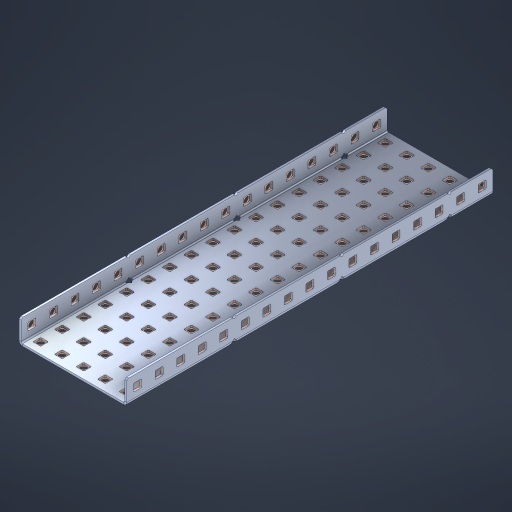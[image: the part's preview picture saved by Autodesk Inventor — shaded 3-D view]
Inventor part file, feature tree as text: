
AUTODESK INVENTOR PART (.ipt)
format: ipt  version: 2023 (Build 270158000, 158)  size: 1,493,504 bytes
history: native  units: in
note: dims shown in document units (in); Inventor stores cm internally (conversion verified against a paired STEP export)
features: other x124, extrude x118, sheet_metal_op x10, sketch x8, mirror x1, pattern_linear x1, chamfer x1
ambient origin geometry x8: Origin, YZ Plane, XZ Plane, XY Plane, X Axis, Y Axis, Z Axis, Center Point
bodies: Solid1 (feature_tree), Body (feature_tree)
feature tree (263):
  other  "Flange Pattern Plane"
  sheet_metal_op  "Flange Pattern"
  sheet_metal_op  "Body Pattern"
  other  "Arc Length"
  mirror  "Notch Mirror"
  pattern_linear  "Notch Pattern"  Spacing1=0.1875in  [1 undecoded]
  chamfer  "End Chamfer"
  extrude  "Half Cut"  Depth=0.0469in
  sketch  "Sketch1"  dims[d0=2.5in]
  other  "Plate1"
  sketch  "Sketch2"  dims[d1=8.5in]
  other  "Plate2"
  sheet_metal_op  "Bend1"
  sheet_metal_op  "Corner1"
  sketch  "Sketch3"  dims[d2=0.0469in]
  other  "Flange Pattern Sketch"
  sketch  "Sketch7"  dims[d3=0.0469in]
  other  "Srf1"
  other  "Srf2"
  sketch  "Sketch8"  dims[d4=0.0234in]
  sketch  "Sketch9"  dims[d5=0.0938in]
  other  "Srf91"
  sheet_metal_op  "Body Pattern Sketch"
  other  "Srf92"
  sketch  "Sketch13"  dims[d6=0.0469in]
  sketch  "Sketch14"  dims[d7=0.5in d8=90.0deg d9=0.0312in d10=0.1875in d11=0.0469in d12=0.0469in d16=0.182in d17=0.02in d18=0.0469in d19=0.0in d20=0.25in d21=0.25in d46=0.172in d47=1.0in d48=0.0in d49=0.182in d50=0.02in d51=0.25in d52=0.25in d53=0.0469in d54=0.0in d55=0.172in d56=1.0in d57=0.0in d60=6.6929in d62=0.5in d63=1.9685in d65=0.5in d85=0.1227in d86=0.1659in d88=0.04in d89=0.0469in d90=0.0in d91=0.04in d92=0.0491in d95=2.5in d96=0.04in d97=0.25in d98=45.0deg d101=0.0in d102=2.497in d131=2.5in d132=6.6929in d134=0.5in d139=0.5in]
  other  "Srf856"
  other  "Srf1310"
  other  "Srf1311"
  other  "Srf1312"
  other  "Srf1376"
  other  "Srf1377"
  other  "Srf1728"
  other  "Srf1755"
  other  "Srf1878"
  other  "Srf1879"
  other  "Srf1880"
  other  "Srf1881"
  other  "Srf1882"
  other  "Srf1883"
  other  "Srf1884"
  other  "Srf1885"
  other  "Srf1886"
  other  "Srf1887"
  other  "Srf1888"
  other  "Srf1889"
  other  "Srf1890"
  other  "Srf1891"
  other  "Srf1892"
  other  "Srf1893"
  other  "Srf1894"
  other  "Srf1895"
  other  "Srf1896"
  other  "Srf1897"
  other  "Srf1898"
  other  "Srf1899"
  other  "Srf1900"
  other  "Srf1901"
  other  "Srf1902"
  other  "Srf1903"
  other  "Srf1904"
  other  "Srf1905"
  other  "Srf1942"
  other  "Srf1943"
  other  "Srf1944"
  other  "Srf1945"
  other  "Srf1946"
  other  "Srf1947"
  other  "Srf1948"
  other  "Srf1949"
  other  "Srf1950"
  other  "Srf1951"
  other  "Srf1952"
  other  "Srf1953"
  other  "Srf1954"
  other  "Srf1955"
  other  "Srf1956"
  other  "Srf1957"
  other  "Srf1958"
  other  "Srf1959"
  other  "Srf1960"
  other  "Srf1961"
  other  "Srf1962"
  other  "Srf1963"
  other  "Srf1964"
  other  "Srf1965"
  other  "Srf1966"
  other  "Srf1967"
  other  "Srf1968"
  other  "Srf1969"
  other  "Srf1970"
  other  "Srf2146"
  other  "Srf2147"
  other  "Srf2148"
  other  "Srf2149"
  other  "Srf2150"
  other  "Srf2151"
  other  "Srf2152"
  other  "Srf2153"
  other  "Srf2154"
  other  "Srf2155"
  other  "Srf2156"
  other  "Srf2157"
  other  "Srf2158"
  other  "Srf2159"
  other  "Srf2160"
  other  "Srf2161"
  other  "Srf2162"
  other  "Srf2163"
  other  "Srf2164"
  other  "Srf2165"
  other  "Srf2166"
  other  "Srf2167"
  other  "Srf2168"
  other  "Srf2169"
  other  "Srf2170"
  other  "Srf2171"
  other  "Srf2172"
  other  "Srf2173"
  other  "Srf2174"
  other  "Srf2175"
  other  "Srf2176"
  other  "Srf2177"
  other  "Srf2178"
  other  "Srf2179"
  other  "Srf2180"
  other  "Srf2181"
  other  "Srf2182"
  other  "Srf2183"
  other  "Srf2184"
  other  "Srf2185"
  other  "Srf2186"
  other  "Srf2187"
  other  "Srf2188"
  other  "Srf2189"
  other  "Srf2190"
  other  "Srf2191"
  other  "Srf2192"
  other  "Srf2193"
  other  "Srf2194"
  other  "Srf2195"
  sheet_metal_op  "Flange Stamp"
  sheet_metal_op  "Flange Circle"
  sheet_metal_op  "Body Stamp"
  sheet_metal_op  "Body Circle"
  sheet_metal_op  "Notch"
  extrude  "ExtrusionSrf2"  Depth=0.0469in
  extrude  "ExtrusionSrf92"  Depth=2.5in
  extrude  "ExtrusionSrf856"  Depth=0.02in
  extrude  "ExtrusionSrf1310"  Depth=0.0469in
  extrude  "ExtrusionSrf1311"  TaperAngle=0.0deg  [1 undecoded]
  extrude  "ExtrusionSrf1312"  Depth=0.25in
  extrude  "ExtrusionSrf1376"  Depth=0.25in
  extrude  "ExtrusionSrf1377"  Depth=2.5in
  extrude  "ExtrusionSrf1728"  Depth=2.5in TaperAngle=0.0deg
  extrude  "ExtrusionSrf1755"  Depth=2.5in
  extrude  "ExtrusionSrf1878"  Depth=0.02in
  extrude  "ExtrusionSrf1879"  Depth=0.25in
  extrude  "ExtrusionSrf1880"  Depth=0.25in
  extrude  "ExtrusionSrf1881"  Depth=0.0469in
  extrude  "ExtrusionSrf1882"  TaperAngle=0.0deg  [1 undecoded]
  extrude  "ExtrusionSrf1883"  Depth=2.5in
  extrude  "ExtrusionSrf1884"  Depth=2.5in TaperAngle=0.0deg
  extrude  "ExtrusionSrf1885"  Depth=2.5in
  extrude  "ExtrusionSrf1886"  Depth=2.5in
  extrude  "ExtrusionSrf1887"  Depth=2.5in
  extrude  "ExtrusionSrf1888"  Depth=2.5in
  extrude  "ExtrusionSrf1889"  Depth=2.5in
  extrude  "ExtrusionSrf1890"  Depth=0.0469in
  extrude  "ExtrusionSrf1891"  TaperAngle=0.0deg  [1 undecoded]
  extrude  "ExtrusionSrf1892"  Depth=2.5in
  extrude  "ExtrusionSrf1893"  Depth=2.5in
  extrude  "ExtrusionSrf1894"  Depth=2.5in
  extrude  "ExtrusionSrf1895"  Depth=0.25in TaperAngle=45.0deg
  extrude  "ExtrusionSrf1896"  TaperAngle=0.0deg  [1 undecoded]
  extrude  "ExtrusionSrf1897"  Depth=2.5in
  extrude  "ExtrusionSrf1898"  Depth=2.5in
  extrude  "ExtrusionSrf1899"  Depth=2.5in
  extrude  "ExtrusionSrf1900"  Depth=2.5in
  extrude  "ExtrusionSrf1901"  Depth=2.5in
  extrude  "ExtrusionSrf1902"  [1 undecoded]
  extrude  "ExtrusionSrf1903"  [1 undecoded]
  extrude  "ExtrusionSrf1904"  [1 undecoded]
  extrude  "ExtrusionSrf1905"  [1 undecoded]
  extrude  "ExtrusionSrf1942"  [1 undecoded]
  extrude  "ExtrusionSrf1943"  [1 undecoded]
  extrude  "ExtrusionSrf1944"  [1 undecoded]
  extrude  "ExtrusionSrf1945"  [1 undecoded]
  extrude  "ExtrusionSrf1946"  [1 undecoded]
  extrude  "ExtrusionSrf1947"  [1 undecoded]
  extrude  "ExtrusionSrf1948"  [1 undecoded]
  extrude  "ExtrusionSrf1949"  [1 undecoded]
  extrude  "ExtrusionSrf1950"  [1 undecoded]
  extrude  "ExtrusionSrf1951"  [1 undecoded]
  extrude  "ExtrusionSrf1952"  [1 undecoded]
  extrude  "ExtrusionSrf1953"  [1 undecoded]
  extrude  "ExtrusionSrf1954"  [1 undecoded]
  extrude  "ExtrusionSrf1955"  [1 undecoded]
  extrude  "ExtrusionSrf1956"  [1 undecoded]
  extrude  "ExtrusionSrf1957"  [1 undecoded]
  extrude  "ExtrusionSrf1958"  [1 undecoded]
  extrude  "ExtrusionSrf1959"  [1 undecoded]
  extrude  "ExtrusionSrf1960"  [1 undecoded]
  extrude  "ExtrusionSrf1961"  [1 undecoded]
  extrude  "ExtrusionSrf1962"  [1 undecoded]
  extrude  "ExtrusionSrf1963"  [1 undecoded]
  extrude  "ExtrusionSrf1964"  [1 undecoded]
  extrude  "ExtrusionSrf1965"  [1 undecoded]
  extrude  "ExtrusionSrf1966"  [1 undecoded]
  extrude  "ExtrusionSrf1967"  [1 undecoded]
  extrude  "ExtrusionSrf1968"  [1 undecoded]
  extrude  "ExtrusionSrf1969"  [1 undecoded]
  extrude  "ExtrusionSrf1970"  [1 undecoded]
  extrude  "ExtrusionSrf2146"  [1 undecoded]
  extrude  "ExtrusionSrf2147"  [1 undecoded]
  extrude  "ExtrusionSrf2148"  [1 undecoded]
  extrude  "ExtrusionSrf2149"  [1 undecoded]
  extrude  "ExtrusionSrf2150"  [1 undecoded]
  extrude  "ExtrusionSrf2151"  [1 undecoded]
  extrude  "ExtrusionSrf2152"  [1 undecoded]
  extrude  "ExtrusionSrf2153"  [1 undecoded]
  extrude  "ExtrusionSrf2154"  [1 undecoded]
  extrude  "ExtrusionSrf2155"  [1 undecoded]
  extrude  "ExtrusionSrf2156"  [1 undecoded]
  extrude  "ExtrusionSrf2157"  [1 undecoded]
  extrude  "ExtrusionSrf2158"  [1 undecoded]
  extrude  "ExtrusionSrf2159"  [1 undecoded]
  extrude  "ExtrusionSrf2160"  [1 undecoded]
  extrude  "ExtrusionSrf2161"  [1 undecoded]
  extrude  "ExtrusionSrf2162"  [1 undecoded]
  extrude  "ExtrusionSrf2163"  [1 undecoded]
  extrude  "ExtrusionSrf2164"  [1 undecoded]
  extrude  "ExtrusionSrf2165"  [1 undecoded]
  extrude  "ExtrusionSrf2166"  [1 undecoded]
  extrude  "ExtrusionSrf2167"  [1 undecoded]
  extrude  "ExtrusionSrf2168"  [1 undecoded]
  extrude  "ExtrusionSrf2169"  [1 undecoded]
  extrude  "ExtrusionSrf2170"  [1 undecoded]
  extrude  "ExtrusionSrf2171"  [1 undecoded]
  extrude  "ExtrusionSrf2172"  [1 undecoded]
  extrude  "ExtrusionSrf2173"  [1 undecoded]
  extrude  "ExtrusionSrf2174"  [1 undecoded]
  extrude  "ExtrusionSrf2175"  [1 undecoded]
  extrude  "ExtrusionSrf2176"  [1 undecoded]
  extrude  "ExtrusionSrf2177"  [1 undecoded]
  extrude  "ExtrusionSrf2178"  [1 undecoded]
  extrude  "ExtrusionSrf2179"  [1 undecoded]
  extrude  "ExtrusionSrf2180"  [1 undecoded]
  extrude  "ExtrusionSrf2181"  [1 undecoded]
  extrude  "ExtrusionSrf2182"  [1 undecoded]
  extrude  "ExtrusionSrf2183"  [1 undecoded]
  extrude  "ExtrusionSrf2184"  [1 undecoded]
  extrude  "ExtrusionSrf2185"  [1 undecoded]
  extrude  "ExtrusionSrf2186"  [1 undecoded]
  extrude  "ExtrusionSrf2187"  [1 undecoded]
  extrude  "ExtrusionSrf2188"  [1 undecoded]
  extrude  "ExtrusionSrf2189"  [1 undecoded]
  extrude  "ExtrusionSrf2190"  [1 undecoded]
  extrude  "ExtrusionSrf2191"  [1 undecoded]
  extrude  "ExtrusionSrf2192"  [1 undecoded]
  extrude  "ExtrusionSrf2193"  [1 undecoded]
  extrude  "ExtrusionSrf2194"  [1 undecoded]
  extrude  "ExtrusionSrf2195"  [1 undecoded]
note: 88 required parameter values undecoded (feature->parameter linkage not recoverable at this tier; creation-order binding heuristic only, values carry confidence <= 0.55)
